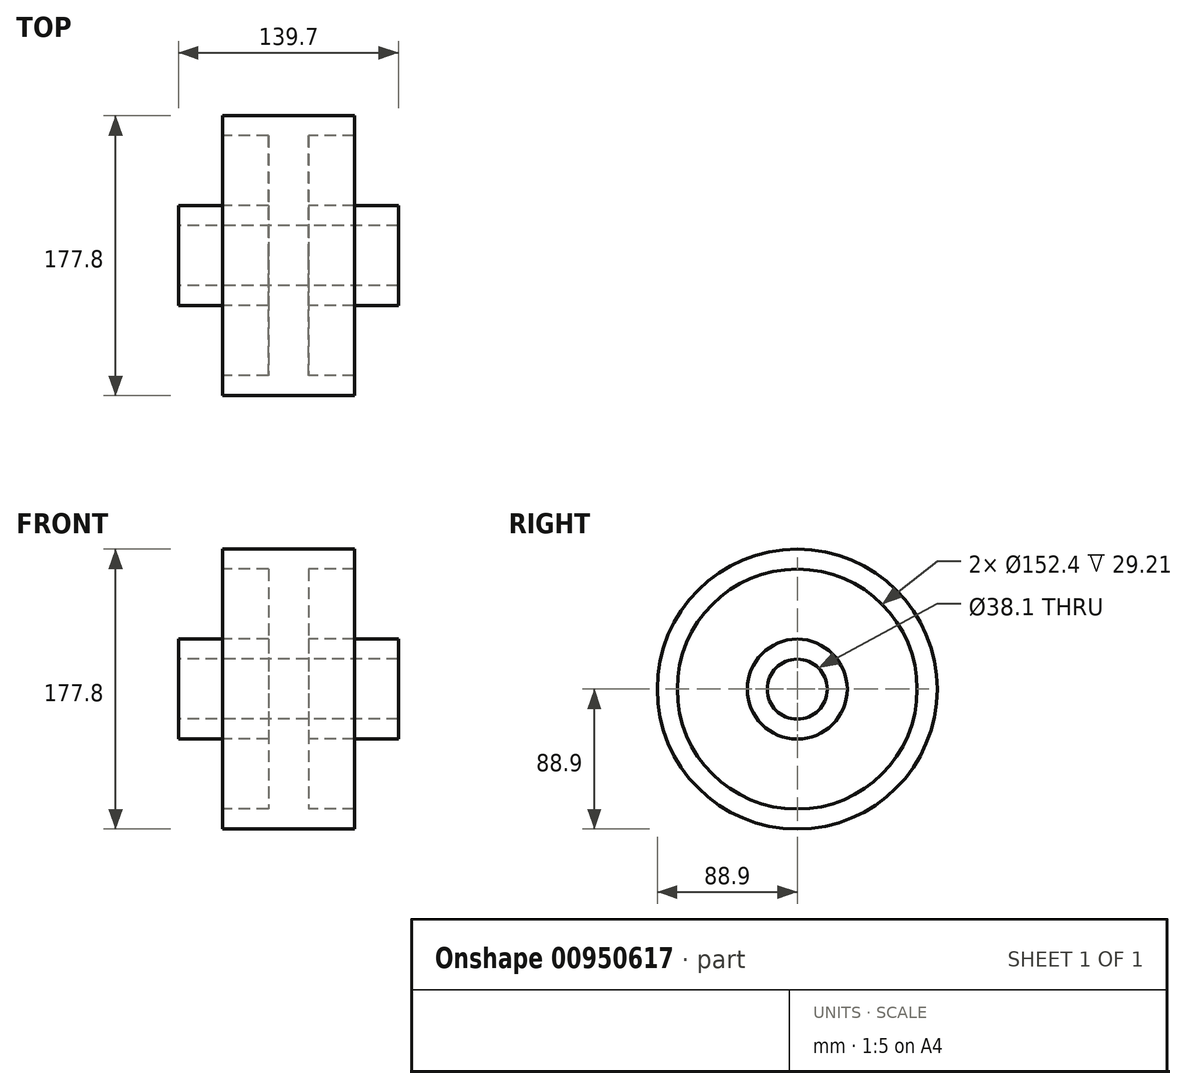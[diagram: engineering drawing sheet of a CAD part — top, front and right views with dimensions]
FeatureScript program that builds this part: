
annotation { "Feature Type Name" : "Feature", "Feature Type Description" : "" }
export const myFeature = defineFeature(function(context is Context, id is Id, definition is map)
    precondition{}
    {
        {
            var Q0;
            Q0=qCreatedBy(makeId("Front.planeOp"),FACE);
            var sketch = newSketch(context, id + "F0", { "sketchPlane" : qUnion([Q0])});
            skLineSegment(sketch, "E0", {"start": v(-112.1, 0) * mm, "end": v(109.28, 0) * mm, "construction": true});
            skLineSegment(sketch, "E1", {"start": v(-69.85, 19.05) * mm, "end": v(69.85, 19.05) * mm});
            skLineSegment(sketch, "E2", {"start": v(69.85, 19.05) * mm, "end": v(69.85, 31.75) * mm});
            skLineSegment(sketch, "E3", {"start": v(69.85, 31.75) * mm, "end": v(12.7, 31.75) * mm});
            skLineSegment(sketch, "E4", {"start": v(12.7, 31.75) * mm, "end": v(12.7, 76.2) * mm});
            skLineSegment(sketch, "E5", {"start": v(12.7, 76.2) * mm, "end": v(41.91, 76.2) * mm});
            skLineSegment(sketch, "E6", {"start": v(41.91, 76.2) * mm, "end": v(41.91, 88.9) * mm});
            skLineSegment(sketch, "E7", {"start": v(41.91, 88.9) * mm, "end": v(-41.91, 88.9) * mm});
            skLineSegment(sketch, "E8", {"start": v(-41.91, 88.9) * mm, "end": v(-41.91, 76.2) * mm});
            skLineSegment(sketch, "E9", {"start": v(-41.91, 76.2) * mm, "end": v(-12.7, 76.2) * mm});
            skLineSegment(sketch, "E10", {"start": v(-12.7, 76.2) * mm, "end": v(-12.7, 31.75) * mm});
            skLineSegment(sketch, "E11", {"start": v(-12.7, 31.75) * mm, "end": v(-69.85, 31.75) * mm});
            skLineSegment(sketch, "E12", {"start": v(-69.85, 31.75) * mm, "end": v(-69.85, 19.05) * mm});
            skLineSegment(sketch, "E13", {"start": v(0, -64.73) * mm, "end": v(0, 114.58) * mm, "construction": true});
            skSolve(sketch);
        }
        {
            var Q0;
            Q0=makeQuery(id+"F0.imprint","IMPRINT",FACE,{"disambiguationData":[TD([[makeQuery(id+"F0.imprint","IMPRINT",EDGE,{"derivedFrom":sQuery(id+"F0.wireOp",EDGE,"E1")}),1.0]])]});
            var Q1;
            Q1=sQuery(id+"F0.wireOp",EDGE,"E0");
            revolve(context, id + "F1", {"surfaceOperationType" : NewSurfaceOperationType.NEW, "entities" : qUnion([Q0]), "axis" : qUnion([Q1]), "revolveType" : RevolveType.FULL});
        }
    });
